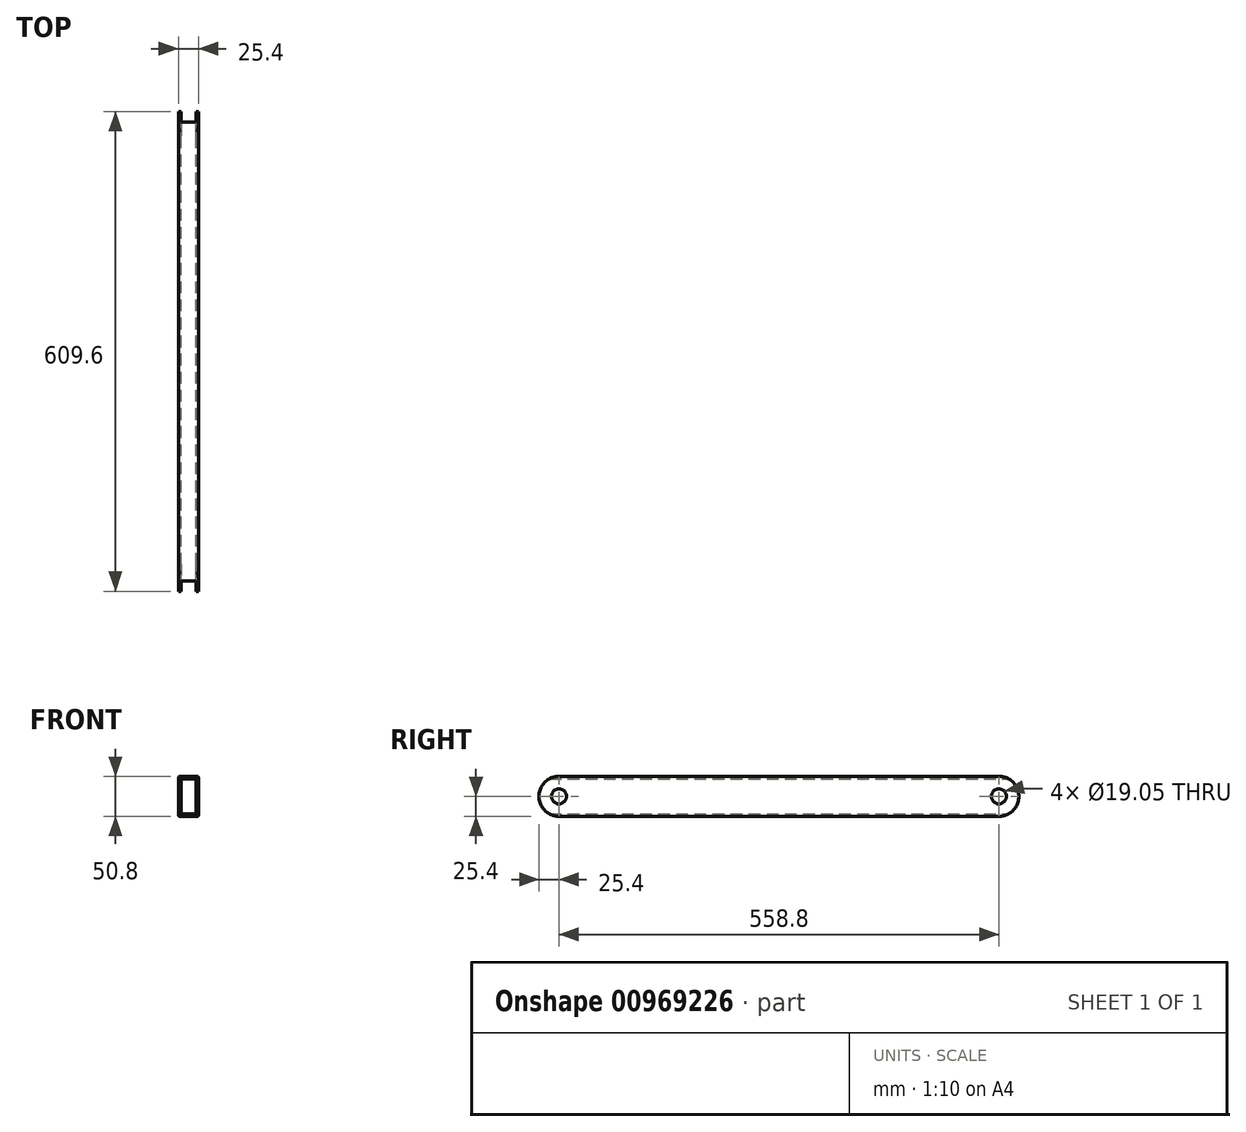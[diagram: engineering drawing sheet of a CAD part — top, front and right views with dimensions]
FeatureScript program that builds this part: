
annotation { "Feature Type Name" : "Feature", "Feature Type Description" : "" }
export const myFeature = defineFeature(function(context is Context, id is Id, definition is map)
    precondition{}
    {
        {
            var Q0;
            Q0=qCreatedBy(makeId("Front.planeOp"),FACE);
            var sketch = newSketch(context, id + "F0", { "sketchPlane" : qUnion([Q0])});
            skLineSegment(sketch, "E0.bottom", {"start": v(11.18, 25.4) * mm, "end": v(-11.18, 25.4) * mm});
            skLineSegment(sketch, "E0.top", {"start": v(11.18, -25.4) * mm, "end": v(-11.18, -25.4) * mm});
            skLineSegment(sketch, "E0.left", {"start": v(12.7, 23.88) * mm, "end": v(12.7, -23.88) * mm});
            skLineSegment(sketch, "E0.right", {"start": v(-12.7, 23.88) * mm, "end": v(-12.7, -23.88) * mm});
            skPoint(sketch, "E0.middle", {"position": v(0, 0) * mm});
            skLineSegment(sketch, "E1.0", {"start": v(8.13, 22.35) * mm, "end": v(-8.13, 22.35) * mm});
            skLineSegment(sketch, "E1.1", {"start": v(9.65, 20.83) * mm, "end": v(9.65, -20.83) * mm});
            skLineSegment(sketch, "E1.2", {"start": v(8.13, -22.35) * mm, "end": v(-8.13, -22.35) * mm});
            skLineSegment(sketch, "E1.3", {"start": v(-9.65, 20.83) * mm, "end": v(-9.65, -20.83) * mm});
            skPoint(sketch, "E2.visualSharp", {"position": v(-12.7, 25.4) * mm});
            skArc(sketch, "E2.filletArc", {"start": v(-11.18, 25.4) * mm, "mid": v(-12.25, 24.95) * mm, "end": v(-12.7, 23.88) * mm});
            skPoint(sketch, "E3.visualSharp", {"position": v(12.7, 25.4) * mm});
            skArc(sketch, "E3.filletArc", {"start": v(12.7, 23.88) * mm, "mid": v(12.25, 24.95) * mm, "end": v(11.18, 25.4) * mm});
            skPoint(sketch, "E4.visualSharp", {"position": v(12.7, -25.4) * mm});
            skArc(sketch, "E4.filletArc", {"start": v(11.18, -25.4) * mm, "mid": v(12.25, -24.95) * mm, "end": v(12.7, -23.88) * mm});
            skPoint(sketch, "E5.visualSharp", {"position": v(-12.7, -25.4) * mm});
            skArc(sketch, "E5.filletArc", {"start": v(-12.7, -23.88) * mm, "mid": v(-12.25, -24.95) * mm, "end": v(-11.18, -25.4) * mm});
            skPoint(sketch, "E6.visualSharp", {"position": v(-9.65, 22.35) * mm});
            skArc(sketch, "E6.filletArc", {"start": v(-8.13, 22.35) * mm, "mid": v(-9.2, 21.9) * mm, "end": v(-9.65, 20.83) * mm});
            skPoint(sketch, "E7.visualSharp", {"position": v(9.65, 22.35) * mm});
            skArc(sketch, "E7.filletArc", {"start": v(9.65, 20.83) * mm, "mid": v(9.2, 21.9) * mm, "end": v(8.13, 22.35) * mm});
            skPoint(sketch, "E8.visualSharp", {"position": v(-9.65, -22.35) * mm});
            skArc(sketch, "E8.filletArc", {"start": v(-9.65, -20.83) * mm, "mid": v(-9.2, -21.9) * mm, "end": v(-8.13, -22.35) * mm});
            skPoint(sketch, "E9.visualSharp", {"position": v(9.65, -22.35) * mm});
            skArc(sketch, "E9.filletArc", {"start": v(8.13, -22.35) * mm, "mid": v(9.2, -21.9) * mm, "end": v(9.65, -20.83) * mm});
            skSolve(sketch);
        }
        {
            var Q0;
            Q0 = qSketchRegion(id + "F0", true);
            extrude(context, id + "F1", {"entities" : qUnion([Q0]), "endBound" : BoundingType.SYMMETRIC, "depth" : 609.6 * mm, "offsetDistance" : 25.4 * mm});
        }
        {
            var Q0;
            Q0=makeQuery(id+"F1.opExtrude","SWEPT_FACE",FACE,{"disambiguationData":[OSD([sQuery(id+"F0.wireOp",EDGE,"E0.left")])]});
            var sketch = newSketch(context, id + "F2", { "sketchPlane" : qUnion([Q0])});
            skCircle(sketch, "E10", {"center": v(-279.4, 0) * mm, "radius": 9.53 * mm});
            skPoint(sketch, "E10.centerSnap0", {"position": v(-304.8, 0) * mm});
            skCircle(sketch, "E11.MirrorC", {"center": v(279.4, 0) * mm, "radius": 9.53 * mm});
            skSolve(sketch);
        }
        {
            var Q0;
            Q0 = qSketchRegion(id + "F2", true);
            extrude(context, id + "F3", {"entities" : qUnion([Q0]), "operationType" : NewBodyOperationType.REMOVE, "oppositeDirection" : true, "depth" : 25.4 * mm, "offsetDistance" : 25.4 * mm});
        }
        {
            var Q0;
            Q0=makeQuery(id+"F1.opExtrude","SWEPT_FACE",FACE,{"disambiguationData":[OSD([sQuery(id+"F0.wireOp",EDGE,"E0.left")])]});
            var sketch = newSketch(context, id + "F4", { "sketchPlane" : qUnion([Q0])});
            skArc(sketch, "E12", {"start": v(-279.4, 25.4) * mm, "mid": v(-304.8, 0) * mm, "end": v(-279.4, -25.4) * mm});
            skLineSegment(sketch, "E13", {"start": v(-279.4, 25.4) * mm, "end": v(-279.4, 43.21) * mm});
            skLineSegment(sketch, "E14", {"start": v(-279.4, 43.21) * mm, "end": v(-315.06, 43.21) * mm});
            skLineSegment(sketch, "E15", {"start": v(-315.06, 43.21) * mm, "end": v(-315.06, -40.74) * mm});
            skLineSegment(sketch, "E16", {"start": v(-315.06, -40.74) * mm, "end": v(-279.4, -40.74) * mm});
            skLineSegment(sketch, "E17", {"start": v(-279.4, -40.74) * mm, "end": v(-279.4, -25.4) * mm});
            skLineSegment(sketch, "E18.MirrorCS", {"start": v(315.06, 43.21) * mm, "end": v(315.06, -40.74) * mm});
            skLineSegment(sketch, "E19.MirrorCS", {"start": v(279.4, 43.21) * mm, "end": v(315.06, 43.21) * mm});
            skLineSegment(sketch, "E20.MirrorCS", {"start": v(279.4, 25.4) * mm, "end": v(279.4, 43.21) * mm});
            skLineSegment(sketch, "E21.MirrorCS", {"start": v(315.06, -40.74) * mm, "end": v(279.4, -40.74) * mm});
            skLineSegment(sketch, "E22.MirrorCS", {"start": v(279.4, -40.74) * mm, "end": v(279.4, -25.4) * mm});
            skArc(sketch, "E23.MirrorCS", {"start": v(279.4, 25.4) * mm, "mid": v(304.8, 0) * mm, "end": v(279.4, -25.4) * mm});
            skSolve(sketch);
        }
        {
            var Q0;
            Q0 = qSketchRegion(id + "F4", true);
            extrude(context, id + "F5", {"entities" : qUnion([Q0]), "operationType" : NewBodyOperationType.REMOVE, "oppositeDirection" : true, "depth" : 25.4 * mm, "offsetDistance" : 25.4 * mm});
        }
    });
